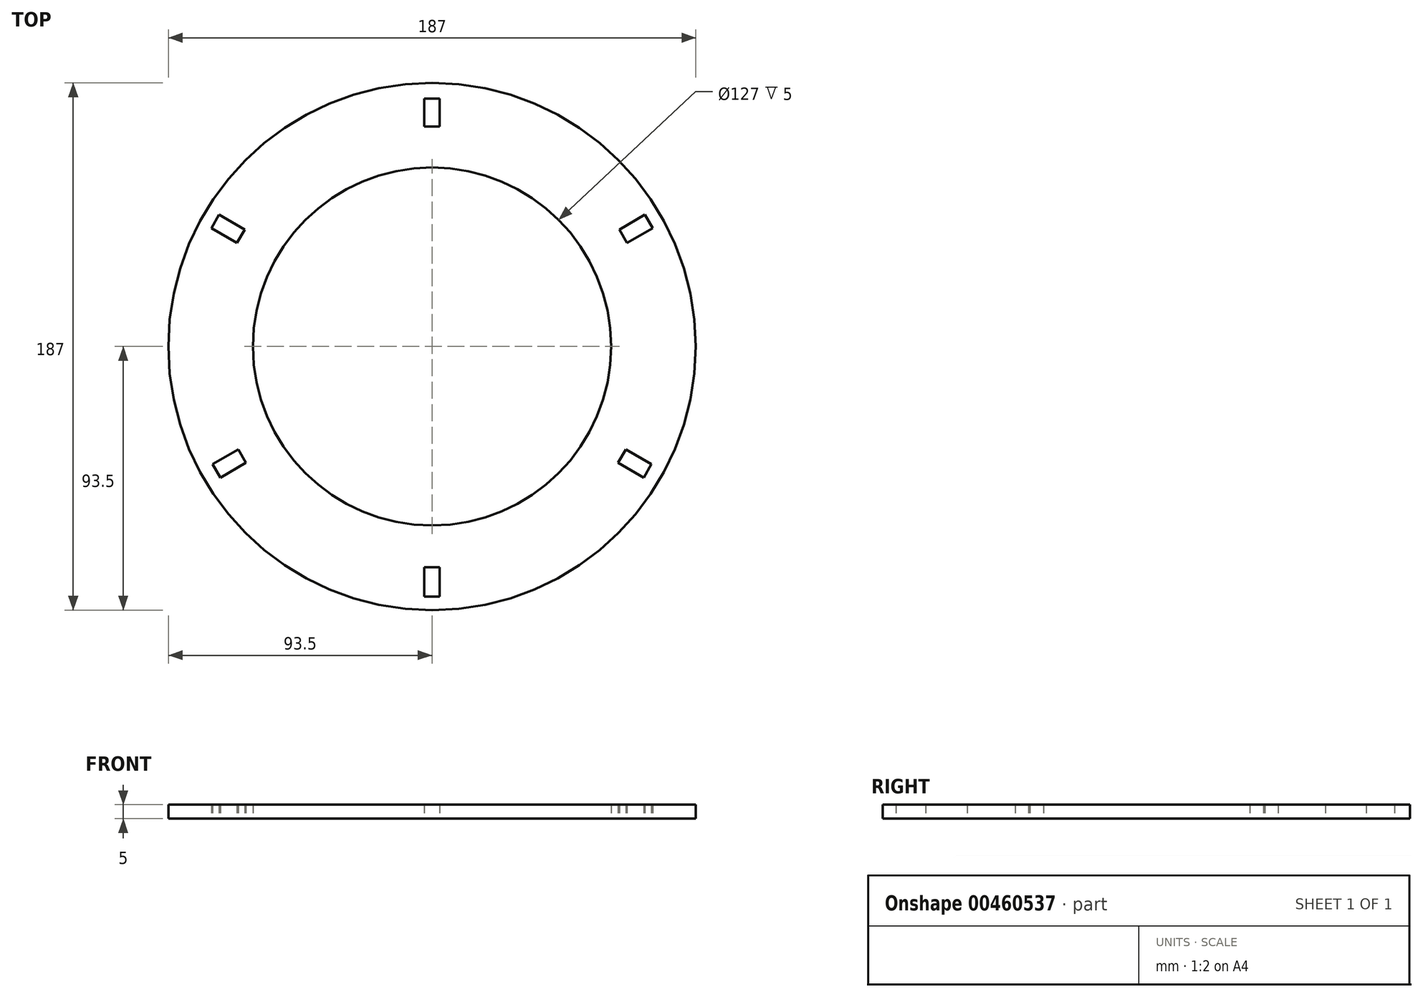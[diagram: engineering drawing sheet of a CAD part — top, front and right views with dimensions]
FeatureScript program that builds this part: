
annotation { "Feature Type Name" : "Feature", "Feature Type Description" : "" }
export const myFeature = defineFeature(function(context is Context, id is Id, definition is map)
    precondition{}
    {
        {
            var Q0;
            Q0=qCreatedBy(makeId("Top.planeOp"),FACE);
            var sketch = newSketch(context, id + "F0", { "sketchPlane" : qUnion([Q0])});
            skCircle(sketch, "E0", {"center": v(0, 0) * mm, "radius": 63.5 * mm});
            skCircle(sketch, "E1", {"center": v(0, 0) * mm, "radius": 93.5 * mm});
            skPoint(sketch, "E2", {"position": v(0, 63.5) * mm});
            skPoint(sketch, "E3", {"position": v(0, -63.5) * mm});
            skPoint(sketch, "E4", {"position": v(63.5, 0) * mm});
            skPoint(sketch, "E5", {"position": v(-63.5, 0) * mm});
            skPoint(sketch, "E6", {"position": v(93.5, 0) * mm});
            skPoint(sketch, "E7", {"position": v(0, 93.5) * mm});
            skPoint(sketch, "E8", {"position": v(-93.5, 0) * mm});
            skPoint(sketch, "E9", {"position": v(0, -93.5) * mm});
            skPoint(sketch, "E10", {"position": v(0, 83) * mm});
            skPoint(sketch, "E11", {"position": v(0, -83.5) * mm});
            skLineSegment(sketch, "E12.bottom", {"start": v(2.75, 78) * mm, "end": v(-2.75, 78) * mm});
            skLineSegment(sketch, "E12.top", {"start": v(2.75, 88) * mm, "end": v(-2.75, 88) * mm});
            skLineSegment(sketch, "E12.left", {"start": v(2.75, 78) * mm, "end": v(2.75, 88) * mm});
            skLineSegment(sketch, "E12.right", {"start": v(-2.75, 78) * mm, "end": v(-2.75, 88) * mm});
            skLineSegment(sketch, "E13.bottom", {"start": v(-2.75, -78.25) * mm, "end": v(2.75, -78.25) * mm});
            skLineSegment(sketch, "E13.top", {"start": v(-2.75, -88.75) * mm, "end": v(2.75, -88.75) * mm});
            skLineSegment(sketch, "E13.left", {"start": v(-2.75, -78.25) * mm, "end": v(-2.75, -88.75) * mm});
            skLineSegment(sketch, "E13.right", {"start": v(2.75, -78.25) * mm, "end": v(2.75, -88.75) * mm});
            skLineSegment(sketch, "E14", {"start": v(0, 0) * mm, "end": v(-71.88, -41.5) * mm, "construction": true});
            skLineSegment(sketch, "E15", {"start": v(0, 0) * mm, "end": v(71.88, -41.5) * mm, "construction": true});
            skLineSegment(sketch, "E16", {"start": v(0, 0) * mm, "end": v(0, 83) * mm, "construction": true});
            skLineSegment(sketch, "E17", {"start": v(-68.7, -36.5) * mm, "end": v(-77.8, -41.74) * mm});
            skLineSegment(sketch, "E18", {"start": v(-77.8, -41.74) * mm, "end": v(-75.05, -46.5) * mm});
            skLineSegment(sketch, "E19", {"start": v(-75.05, -46.5) * mm, "end": v(-65.96, -41.26) * mm});
            skLineSegment(sketch, "E20", {"start": v(-65.96, -41.26) * mm, "end": v(-68.7, -36.5) * mm});
            skPoint(sketch, "E21", {"position": v(-73.26, -39.12) * mm});
            skPoint(sketch, "E22", {"position": v(-70.5, -43.88) * mm});
            skLineSegment(sketch, "E23", {"start": v(-73.26, -39.12) * mm, "end": v(-70.5, -43.88) * mm, "construction": true});
            skLineSegment(sketch, "E24.MirrorCS", {"start": v(68.7, -36.5) * mm, "end": v(77.8, -41.74) * mm});
            skLineSegment(sketch, "E25.MirrorCS", {"start": v(77.8, -41.74) * mm, "end": v(75.05, -46.5) * mm});
            skLineSegment(sketch, "E26.MirrorCS", {"start": v(75.05, -46.5) * mm, "end": v(65.96, -41.26) * mm});
            skLineSegment(sketch, "E27.MirrorCS", {"start": v(65.96, -41.26) * mm, "end": v(68.7, -36.5) * mm});
            skLineSegment(sketch, "E28", {"start": v(0, 0) * mm, "end": v(0, -83.5) * mm, "construction": true});
            skLineSegment(sketch, "E29", {"start": v(0, 0) * mm, "end": v(71.88, 41.5) * mm, "construction": true});
            skLineSegment(sketch, "E30", {"start": v(0, 0) * mm, "end": v(-71.88, 41.5) * mm, "construction": true});
            skLineSegment(sketch, "E31.MirrorCS", {"start": v(66.4, 41.5) * mm, "end": v(69.14, 36.74) * mm});
            skLineSegment(sketch, "E32.MirrorCS", {"start": v(66.4, 41.5) * mm, "end": v(75.48, 46.76) * mm});
            skLineSegment(sketch, "E33.MirrorCS", {"start": v(69.14, 36.74) * mm, "end": v(78.23, 42) * mm});
            skLineSegment(sketch, "E34.MirrorCS", {"start": v(75.48, 46.76) * mm, "end": v(78.23, 42) * mm});
            skLineSegment(sketch, "E35.MirrorCS", {"start": v(-69.14, 36.74) * mm, "end": v(-66.4, 41.5) * mm});
            skLineSegment(sketch, "E36.MirrorCS", {"start": v(-78.23, 42) * mm, "end": v(-75.48, 46.76) * mm});
            skLineSegment(sketch, "E37.MirrorCS", {"start": v(-69.14, 36.74) * mm, "end": v(-78.23, 42) * mm});
            skLineSegment(sketch, "E38.MirrorCS", {"start": v(-66.4, 41.5) * mm, "end": v(-75.48, 46.76) * mm});
            skPoint(sketch, "E39", {"position": v(-67.33, -38.87) * mm});
            skPoint(sketch, "E40", {"position": v(-58.46, -33.75) * mm});
            skPoint(sketch, "E41", {"position": v(-76.21, -44) * mm});
            skLineSegment(sketch, "E42", {"start": v(-71.88, -41.5) * mm, "end": v(-76.43, -44.12) * mm, "construction": true});
            skSolve(sketch);
        }
        {
            var Q0;
            Q0=makeQuery(id+"F0.imprint","IMPRINT",FACE,{"disambiguationData":[TD([[makeQuery(id+"F0.imprint","IMPRINT",EDGE,{"derivedFrom":sQuery(id+"F0.wireOp",EDGE,"E0")}),-1.0]])]});
            extrude(context, id + "F1", {"entities" : qUnion([Q0]), "depth" : 5 * mm});
        }
    });
